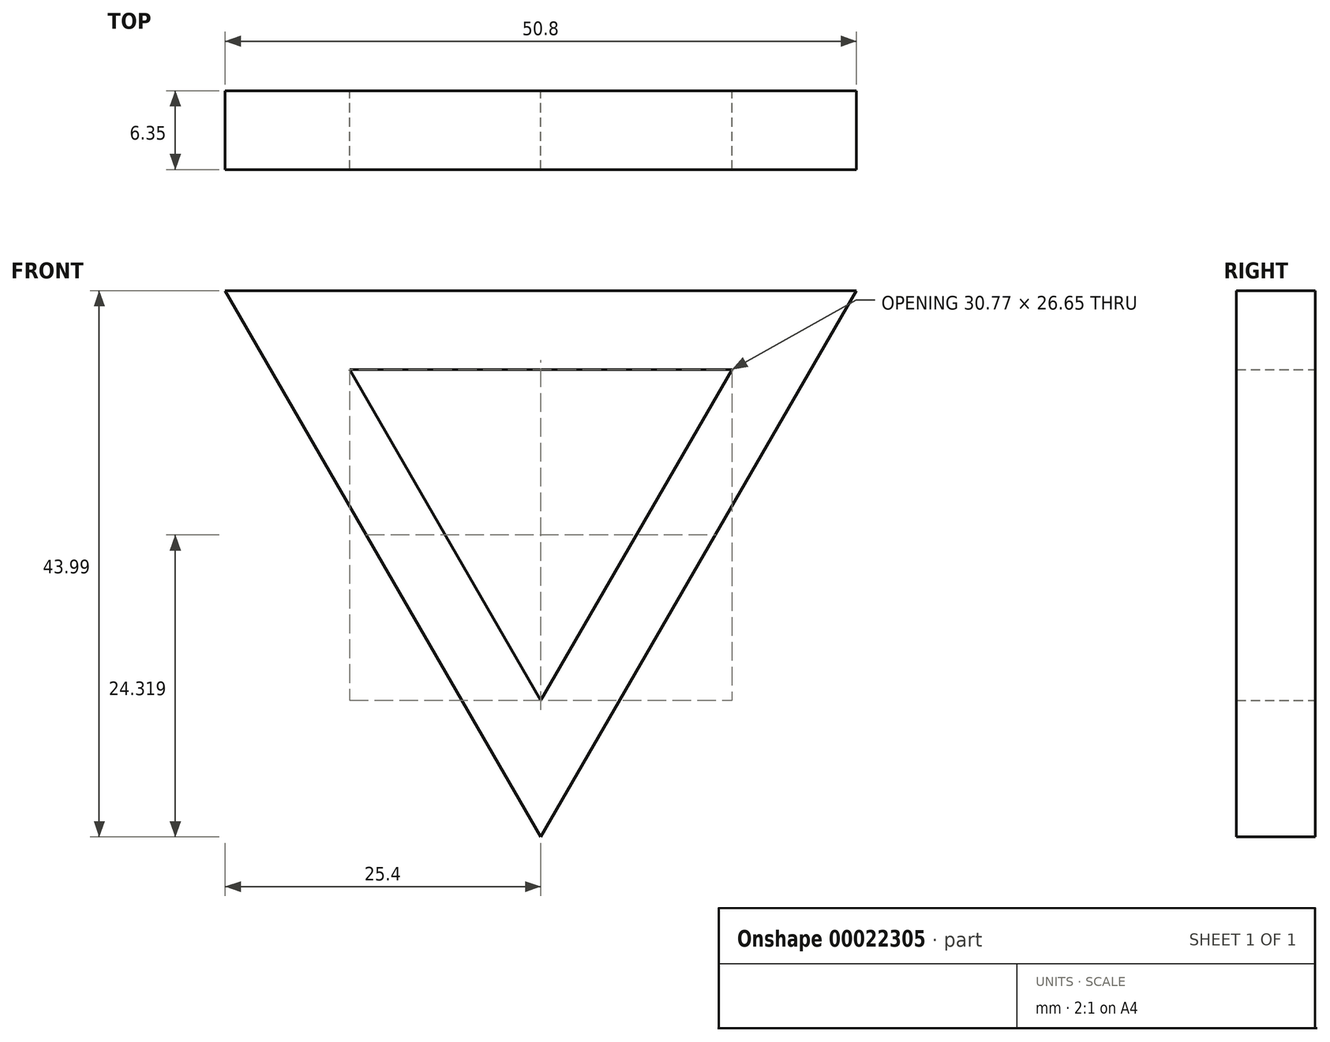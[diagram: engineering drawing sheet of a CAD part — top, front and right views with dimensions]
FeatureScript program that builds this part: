
annotation { "Feature Type Name" : "Feature", "Feature Type Description" : "" }
export const myFeature = defineFeature(function(context is Context, id is Id, definition is map)
    precondition{}
    {
        {
            var Q0;
            Q0=qCreatedBy(makeId("Front.planeOp"),FACE);
            var sketch = newSketch(context, id + "F0", { "sketchPlane" : qUnion([Q0])});
            skLineSegment(sketch, "E0", {"start": v(-25.4, 22.67) * mm, "end": v(25.4, 22.67) * mm});
            skLineSegment(sketch, "E1", {"start": v(-25.4, 22.67) * mm, "end": v(0, -21.32) * mm});
            skLineSegment(sketch, "E2", {"start": v(0, -21.32) * mm, "end": v(25.4, 22.67) * mm});
            skLineSegment(sketch, "E3", {"start": v(0, 22.67) * mm, "end": v(0, 16.32) * mm});
            skLineSegment(sketch, "E4", {"start": v(-5.96, 0) * mm, "end": v(-15.38, 16.32) * mm});
            skLineSegment(sketch, "E5", {"start": v(-5.96, 0) * mm, "end": v(0, -10.32) * mm});
            skLineSegment(sketch, "E6", {"start": v(5.96, 0) * mm, "end": v(15.38, 16.32) * mm});
            skLineSegment(sketch, "E7", {"start": v(5.96, 0) * mm, "end": v(0, -10.32) * mm});
            skLineSegment(sketch, "E8.trimOffspring", {"start": v(-15.38, 16.32) * mm, "end": v(15.38, 16.32) * mm});
            skPoint(sketch, "E9.start.orphan", {"position": v(-12.31, 0) * mm});
            skPoint(sketch, "E10.start.orphan", {"position": v(-33.67, 16.32) * mm});
            skPoint(sketch, "E11.trimOffspring.end.orphan", {"position": v(25.4, 33.67) * mm});
            skSolve(sketch);
        }
        {
            var Q0;
            Q0 = qSketchRegion(id + "F0", true);
            extrude(context, id + "F1", {"entities" : qUnion([Q0]), "depth" : 6.35 * mm});
        }
    });
